# Revit family: LXMMPED
name_source: partatom
category: Modelos genéricos
units: mm (PartAtom-declared; Revit-internal decimal feet)

## family parameters
Com base no plano de trabalho = Não
Compartilhado = Sim
Corte com vazios quando carregada = Não
Cota do conector redondo = Utilizar diâmetro
Número OmniClass = 23.60.00.00
Pode hospedar o vergalhão = Não
Ponto de cálculo do ambiente = Não
Sempre na vertical = Sim
Tipo de parte = Normal
Título OmniClass = General Purpose: Services

## types (1)
- LXMMPED
    Comentários de tipos = LXMMPED
    Elevação padrão = 0  [stored 0 ft]
    Modelo = LXMMPED
    RainBird: Code = F42410
    RainBird: Description = LXMMPED
    RainBird: Product Link = www.rainbird.com
    SupportProjetos: Level of Detail = LOD300
    SupportProjetos: Review = R00
    URL = www.rainbird.com
    es = 152  [stored 0.498688 ft]
    h = 798  [stored 2.61811 ft]
    l = 384  [stored 1.25984 ft]

note: [stored X ft] marks values corroborated as IEEE doubles in the binary element streams (Revit-internal decimal feet)
